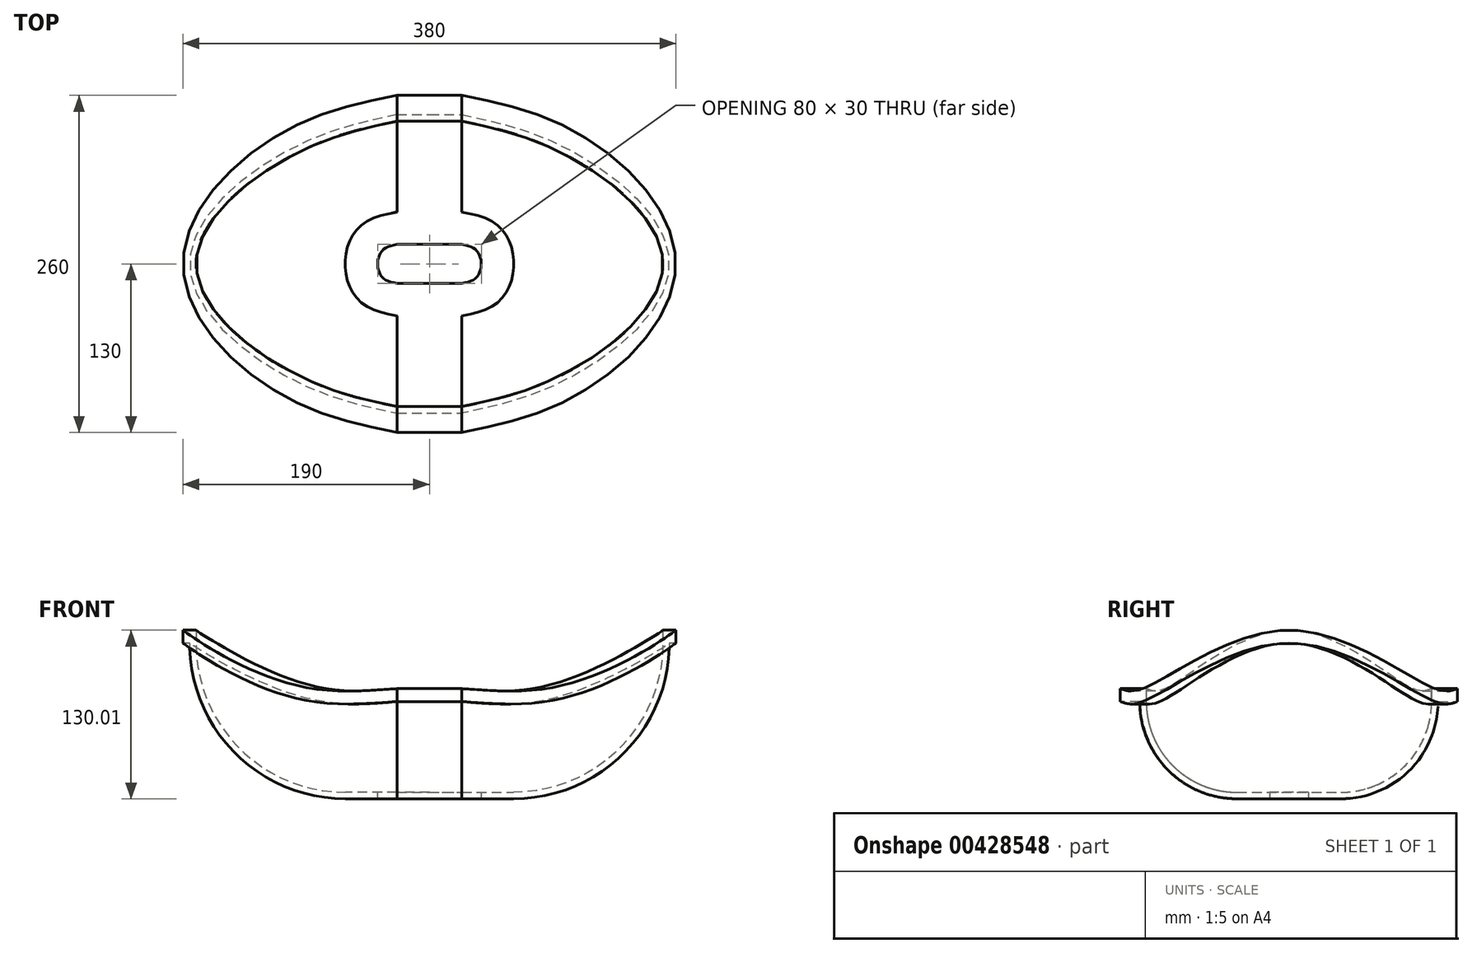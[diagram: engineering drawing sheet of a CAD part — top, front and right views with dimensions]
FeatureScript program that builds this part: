
annotation { "Feature Type Name" : "Feature", "Feature Type Description" : "" }
export const myFeature = defineFeature(function(context is Context, id is Id, definition is map)
    precondition{}
    {
        {
            var Q0;
            Q0=qCreatedBy(makeId("Front.planeOp"),FACE);
            var sketch = newSketch(context, id + "F0", { "sketchPlane" : qUnion([Q0])});
            skLineSegment(sketch, "E0.bottom", {"start": v(15, 5) * mm, "end": v(40, 5) * mm});
            skLineSegment(sketch, "E0.top", {"start": v(15, 0) * mm, "end": v(40, 0) * mm});
            skLineSegment(sketch, "E0.left", {"start": v(15, 5) * mm, "end": v(15, 0) * mm});
            skLineSegment(sketch, "E0.right", {"start": v(40, 5) * mm, "end": v(40, 0) * mm, "construction": true});
            skLineSegment(sketch, "E1.bottom", {"start": v(155, 130) * mm, "end": v(165, 130) * mm});
            skLineSegment(sketch, "E1.top", {"start": v(160, 120) * mm, "end": v(165, 120) * mm});
            skLineSegment(sketch, "E1.left", {"start": v(155, 130) * mm, "end": v(155, 120) * mm});
            skLineSegment(sketch, "E1.right", {"start": v(165, 130) * mm, "end": v(165, 120) * mm});
            skArc(sketch, "E2", {"start": v(40, 5) * mm, "mid": v(121.32, 38.68) * mm, "end": v(155, 120) * mm});
            skArc(sketch, "E3", {"start": v(40, 0) * mm, "mid": v(124.85, 35.15) * mm, "end": v(160, 120) * mm});
            skLineSegment(sketch, "E4", {"start": v(0, 0) * mm, "end": v(0, 50) * mm, "construction": true});
            skSolve(sketch);
        }
        {
            var Q0;
            Q0=sQuery(id+"F0.wireOp",EDGE,"E4");
            cPlane(context, id + "F1", {"entities" : qUnion([Q0]), "cplaneType" : CPlaneType.LINE_ANGLE, "offset" : 25 * mm, "angle" : 30 * degree, "oppositeDirection" : true, "width" : 150 * mm, "height" : 150 * mm});
        }
        {
            var Q0;
            Q0=qCreatedBy(id+"F1.planeOp",FACE);
            var sketch = newSketch(context, id + "F2", { "sketchPlane" : qUnion([Q0])});
            skLineSegment(sketch, "E5.bottom", {"start": v(15, 5) * mm, "end": v(40, 5) * mm});
            skLineSegment(sketch, "E5.top", {"start": v(15, 0) * mm, "end": v(40, 0) * mm});
            skLineSegment(sketch, "E5.left", {"start": v(15, 5) * mm, "end": v(15, 0) * mm});
            skLineSegment(sketch, "E5.right", {"start": v(40, 5) * mm, "end": v(40, 0) * mm, "construction": true});
            skLineSegment(sketch, "E6.bottom", {"start": v(110, 85) * mm, "end": v(130, 85) * mm});
            skLineSegment(sketch, "E6.top", {"start": v(115, 75) * mm, "end": v(130, 75) * mm});
            skLineSegment(sketch, "E6.left", {"start": v(110, 85) * mm, "end": v(110, 75) * mm});
            skLineSegment(sketch, "E6.right", {"start": v(130, 85) * mm, "end": v(130, 75) * mm});
            skArc(sketch, "E7", {"start": v(40, 5) * mm, "mid": v(89.5, 25.5) * mm, "end": v(110, 75) * mm});
            skArc(sketch, "E8", {"start": v(40, 0) * mm, "mid": v(93.03, 21.97) * mm, "end": v(115, 75) * mm});
            skLineSegment(sketch, "E9", {"start": v(0, 0) * mm, "end": v(0, 50) * mm, "construction": true});
            skSolve(sketch);
        }
        {
            var Q0;
            Q0=sQuery(id+"F2.wireOp",EDGE,"E9");
            cPlane(context, id + "F3", {"entities" : qUnion([Q0]), "cplaneType" : CPlaneType.LINE_ANGLE, "offset" : 25 * mm, "angle" : 150 * degree, "oppositeDirection" : true, "width" : 150 * mm, "height" : 150 * mm});
        }
        {
            var Q0;
            Q0=qCreatedBy(id+"F3.planeOp",FACE);
            var sketch = newSketch(context, id + "F4", { "sketchPlane" : qUnion([Q0])});
            skLineSegment(sketch, "E10.bottom", {"start": v(15, 5) * mm, "end": v(40, 5) * mm});
            skLineSegment(sketch, "E10.top", {"start": v(15, 0) * mm, "end": v(40, 0) * mm});
            skLineSegment(sketch, "E10.left", {"start": v(15, 5) * mm, "end": v(15, 0) * mm});
            skLineSegment(sketch, "E10.right", {"start": v(40, 5) * mm, "end": v(40, 0) * mm, "construction": true});
            skLineSegment(sketch, "E11.bottom", {"start": v(110, 85) * mm, "end": v(130, 85) * mm});
            skLineSegment(sketch, "E11.top", {"start": v(115, 75) * mm, "end": v(130, 75) * mm});
            skLineSegment(sketch, "E11.left", {"start": v(110, 85) * mm, "end": v(110, 75) * mm});
            skLineSegment(sketch, "E11.right", {"start": v(130, 85) * mm, "end": v(130, 75) * mm});
            skArc(sketch, "E12", {"start": v(40, 5) * mm, "mid": v(89.5, 25.5) * mm, "end": v(110, 75) * mm});
            skArc(sketch, "E13", {"start": v(40, 0) * mm, "mid": v(93.03, 21.97) * mm, "end": v(115, 75) * mm});
            skLineSegment(sketch, "E14", {"start": v(0, 0) * mm, "end": v(0, 50) * mm, "construction": true});
            skSolve(sketch);
        }
        {
            var Q0;
            Q0=qCreatedBy(makeId("Right.planeOp"),FACE);
            var sketch = newSketch(context, id + "F5", { "sketchPlane" : qUnion([Q0])});
            skLineSegment(sketch, "E15.bottom", {"start": v(15, 5) * mm, "end": v(40, 5) * mm});
            skLineSegment(sketch, "E15.top", {"start": v(15, 0) * mm, "end": v(40, 0) * mm});
            skLineSegment(sketch, "E15.left", {"start": v(15, 5) * mm, "end": v(15, 0) * mm});
            skLineSegment(sketch, "E15.right", {"start": v(40, 5) * mm, "end": v(40, 0) * mm, "construction": true});
            skLineSegment(sketch, "E16.bottom", {"start": v(110, 85) * mm, "end": v(130, 85) * mm});
            skLineSegment(sketch, "E16.top", {"start": v(115, 75) * mm, "end": v(130, 75) * mm});
            skLineSegment(sketch, "E16.left", {"start": v(110, 85) * mm, "end": v(110, 75) * mm});
            skLineSegment(sketch, "E16.right", {"start": v(130, 85) * mm, "end": v(130, 75) * mm});
            skArc(sketch, "E17", {"start": v(40, 5) * mm, "mid": v(89.5, 25.5) * mm, "end": v(110, 75) * mm});
            skArc(sketch, "E18", {"start": v(40, 0) * mm, "mid": v(93.03, 21.97) * mm, "end": v(115, 75) * mm});
            skLineSegment(sketch, "E19", {"start": v(0, 0) * mm, "end": v(0, 50) * mm, "construction": true});
            skSolve(sketch);
        }
        {
            var Q0;
            Q0=sQuery(id+"F5.wireOp",EDGE,"E19");
            cPlane(context, id + "F6", {"entities" : qUnion([Q0]), "cplaneType" : CPlaneType.LINE_ANGLE, "offset" : 25 * mm, "angle" : 180 * degree, "width" : 150 * mm, "height" : 150 * mm});
        }
        {
            var Q0;
            Q0=qCreatedBy(id+"F6.planeOp",FACE);
            var sketch = newSketch(context, id + "F7", { "sketchPlane" : qUnion([Q0])});
            skLineSegment(sketch, "E20.bottom", {"start": v(15, 5) * mm, "end": v(40, 5) * mm});
            skLineSegment(sketch, "E20.top", {"start": v(15, 0) * mm, "end": v(40, 0) * mm});
            skLineSegment(sketch, "E20.left", {"start": v(15, 5) * mm, "end": v(15, 0) * mm});
            skLineSegment(sketch, "E20.right", {"start": v(40, 5) * mm, "end": v(40, 0) * mm, "construction": true});
            skLineSegment(sketch, "E21.bottom", {"start": v(110, 85) * mm, "end": v(130, 85) * mm});
            skLineSegment(sketch, "E21.top", {"start": v(115, 75) * mm, "end": v(130, 75) * mm});
            skLineSegment(sketch, "E21.left", {"start": v(110, 85) * mm, "end": v(110, 75) * mm});
            skLineSegment(sketch, "E21.right", {"start": v(130, 85) * mm, "end": v(130, 75) * mm});
            skArc(sketch, "E22", {"start": v(40, 5) * mm, "mid": v(89.5, 25.5) * mm, "end": v(110, 75) * mm});
            skArc(sketch, "E23", {"start": v(40, 0) * mm, "mid": v(93.03, 21.97) * mm, "end": v(115, 75) * mm});
            skLineSegment(sketch, "E24", {"start": v(0, 0) * mm, "end": v(0, 50) * mm, "construction": true});
            skSolve(sketch);
        }
        {
            var Q0;
            Q0=makeQuery(id+"F5.imprint","IMPRINT",FACE,{"disambiguationData":[TD([[makeQuery(id+"F5.imprint","IMPRINT",EDGE,{"derivedFrom":sQuery(id+"F5.wireOp",EDGE,"E15.bottom")}),-1.0]])]});
            var Q1;
            Q1=makeQuery(id+"F2.imprint","IMPRINT",FACE,{"disambiguationData":[TD([[makeQuery(id+"F2.imprint","IMPRINT",EDGE,{"derivedFrom":sQuery(id+"F2.wireOp",EDGE,"E5.bottom")}),-1.0]])]});
            var Q2;
            Q2=makeQuery(id+"F0.imprint","IMPRINT",FACE,{"disambiguationData":[TD([[makeQuery(id+"F0.imprint","IMPRINT",EDGE,{"derivedFrom":sQuery(id+"F0.wireOp",EDGE,"E0.bottom")}),-1.0]])]});
            var Q3;
            Q3=makeQuery(id+"F4.imprint","IMPRINT",FACE,{"disambiguationData":[TD([[makeQuery(id+"F4.imprint","IMPRINT",EDGE,{"derivedFrom":sQuery(id+"F4.wireOp",EDGE,"E10.bottom")}),-1.0]])]});
            var Q4;
            Q4=makeQuery(id+"F7.imprint","IMPRINT",FACE,{"disambiguationData":[TD([[makeQuery(id+"F7.imprint","IMPRINT",EDGE,{"derivedFrom":sQuery(id+"F7.wireOp",EDGE,"E20.bottom")}),-1.0]])]});
            loft(context, id + "F8", {"sheetProfilesArray" : [{ "sheetProfileEntities" : qUnion([Q0]) }, { "sheetProfileEntities" : qUnion([Q1]) }, { "sheetProfileEntities" : qUnion([Q2]) }, { "sheetProfileEntities" : qUnion([Q3]) }, { "sheetProfileEntities" : qUnion([Q4]) }]});
        }
        {
            var Q0;
            Q0=makeQuery(id+"F8.opLoft","CAP_FACE",FACE,{"disambiguationData":[OSD([makeQuery(id+"F5.imprint","IMPRINT",FACE,{"disambiguationData":[TD([[makeQuery(id+"F5.imprint","IMPRINT",EDGE,{"derivedFrom":sQuery(id+"F5.wireOp",EDGE,"E15.bottom")}),-1.0]])]})])],"isStart":true});
            var sketch = newSketch(context, id + "F9", { "sketchPlane" : qUnion([Q0])});
            skLineSegment(sketch, "E25.0.0", {"start": v(-130, 75) * mm, "end": v(-130, 85) * mm});
            skLineSegment(sketch, "E25.0.1", {"start": v(-130, 75) * mm, "end": v(-115, 75) * mm});
            skFitSpline(sketch, "E25.0.2", {"points": [v(-115, 75) * mm, v(-115, 72.54) * mm, v(-114.88, 70.1) * mm, v(-114.64, 67.65) * mm, v(-114.4, 65.2) * mm, v(-114.04, 62.78) * mm, v(-113.56, 60.37) * mm, v(-113.08, 57.96) * mm, v(-112.48, 55.58) * mm, v(-111.77, 53.23) * mm, v(-111.06, 50.88) * mm, v(-110.23, 48.57) * mm, v(-109.3, 46.3) * mm, v(-108.35, 44.03) * mm, v(-107.3, 41.81) * mm, v(-106.14, 39.65) * mm, v(-104.99, 37.48) * mm, v(-103.73, 35.37) * mm, v(-102.36, 33.33) * mm, v(-101, 31.3) * mm, v(-99.53, 29.32) * mm, v(-97.98, 27.42) * mm, v(-96.42, 25.52) * mm, v(-94.77, 23.7) * mm, v(-93.03, 21.97) * mm, v(-91.3, 20.23) * mm, v(-89.48, 18.58) * mm, v(-87.58, 17.02) * mm, v(-85.68, 15.47) * mm, v(-83.71, 14) * mm, v(-81.67, 12.64) * mm, v(-79.63, 11.28) * mm, v(-77.52, 10.01) * mm, v(-75.35, 8.86) * mm, v(-73.19, 7.7) * mm, v(-70.97, 6.65) * mm, v(-68.7, 5.7) * mm, v(-66.43, 4.77) * mm, v(-64.12, 3.94) * mm, v(-61.77, 3.23) * mm, v(-59.42, 2.52) * mm, v(-57.04, 1.92) * mm, v(-54.63, 1.44) * mm, v(-52.22, 0.96) * mm, v(-49.8, 0.6) * mm, v(-47.35, 0.36) * mm, v(-44.9, 0.12) * mm, v(-42.46, 0) * mm, v(-40, 0) * mm]});
            skLineSegment(sketch, "E25.0.3", {"start": v(-40, 0) * mm, "end": v(-15, 0) * mm});
            skLineSegment(sketch, "E25.0.4", {"start": v(-15, 0) * mm, "end": v(-15, 5) * mm});
            skLineSegment(sketch, "E25.0.5", {"start": v(-40, 5) * mm, "end": v(-15, 5) * mm});
            skFitSpline(sketch, "E25.0.6", {"points": [v(-40, 5) * mm, v(-42.3, 5) * mm, v(-44.58, 5.11) * mm, v(-46.86, 5.34) * mm, v(-49.14, 5.56) * mm, v(-51.4, 5.9) * mm, v(-53.66, 6.35) * mm, v(-55.9, 6.8) * mm, v(-58.13, 7.35) * mm, v(-60.32, 8.01) * mm, v(-62.51, 8.68) * mm, v(-64.67, 9.45) * mm, v(-66.79, 10.33) * mm, v(-68.9, 11.2) * mm, v(-70.98, 12.18) * mm, v(-73, 13.27) * mm, v(-75.02, 14.35) * mm, v(-76.98, 15.52) * mm, v(-78.89, 16.8) * mm, v(-80.8, 18.07) * mm, v(-82.64, 19.43) * mm, v(-84.4, 20.89) * mm, v(-86.18, 22.34) * mm, v(-87.88, 23.88) * mm, v(-89.5, 25.5) * mm, v(-91.12, 27.12) * mm, v(-92.66, 28.82) * mm, v(-94.11, 30.6) * mm, v(-95.56, 32.36) * mm, v(-96.93, 34.2) * mm, v(-98.2, 36.11) * mm, v(-99.48, 38.02) * mm, v(-100.65, 39.98) * mm, v(-101.73, 42) * mm, v(-102.82, 44.02) * mm, v(-103.8, 46.1) * mm, v(-104.67, 48.21) * mm, v(-105.55, 50.33) * mm, v(-106.32, 52.49) * mm, v(-106.99, 54.68) * mm, v(-107.65, 56.87) * mm, v(-108.2, 59.1) * mm, v(-108.65, 61.34) * mm, v(-109.1, 63.6) * mm, v(-109.44, 65.86) * mm, v(-109.66, 68.14) * mm, v(-109.89, 70.42) * mm, v(-110, 72.7) * mm, v(-110, 75) * mm]});
            skFitSpline(sketch, "E25.0.7", {"points": [v(-110, 75) * mm, v(-110, 78.33) * mm, v(-110, 81.67) * mm, v(-110, 85) * mm]});
            skLineSegment(sketch, "E25.0.8", {"start": v(-130, 85) * mm, "end": v(-110, 85) * mm});
            skLineSegment(sketch, "E26.0.0", {"start": v(130, 75) * mm, "end": v(130, 85) * mm});
            skLineSegment(sketch, "E26.0.1", {"start": v(130, 85) * mm, "end": v(110, 85) * mm});
            skFitSpline(sketch, "E26.0.2", {"points": [v(110, 85) * mm, v(110, 81.67) * mm, v(110, 78.33) * mm, v(110, 75) * mm]});
            skFitSpline(sketch, "E26.0.3", {"points": [v(110, 75) * mm, v(110, 72.7) * mm, v(109.89, 70.42) * mm, v(109.66, 68.14) * mm, v(109.44, 65.86) * mm, v(109.1, 63.6) * mm, v(108.65, 61.34) * mm, v(108.2, 59.1) * mm, v(107.65, 56.87) * mm, v(106.99, 54.68) * mm, v(106.32, 52.49) * mm, v(105.55, 50.33) * mm, v(104.67, 48.21) * mm, v(103.8, 46.1) * mm, v(102.82, 44.02) * mm, v(101.73, 42) * mm, v(100.65, 39.98) * mm, v(99.48, 38.02) * mm, v(98.2, 36.11) * mm, v(96.93, 34.2) * mm, v(95.57, 32.36) * mm, v(94.11, 30.6) * mm, v(92.66, 28.82) * mm, v(91.12, 27.12) * mm, v(89.5, 25.5) * mm, v(87.88, 23.88) * mm, v(86.18, 22.34) * mm, v(84.4, 20.89) * mm, v(82.64, 19.44) * mm, v(80.8, 18.07) * mm, v(78.89, 16.8) * mm, v(76.98, 15.52) * mm, v(75.02, 14.35) * mm, v(73, 13.27) * mm, v(70.98, 12.18) * mm, v(68.9, 11.2) * mm, v(66.79, 10.33) * mm, v(64.67, 9.45) * mm, v(62.51, 8.68) * mm, v(60.32, 8.01) * mm, v(58.13, 7.35) * mm, v(55.9, 6.8) * mm, v(53.66, 6.35) * mm, v(51.4, 5.9) * mm, v(49.14, 5.56) * mm, v(46.86, 5.34) * mm, v(44.58, 5.11) * mm, v(42.3, 5) * mm, v(40, 5) * mm]});
            skLineSegment(sketch, "E26.0.4", {"start": v(40, 5) * mm, "end": v(15, 5) * mm});
            skLineSegment(sketch, "E26.0.5", {"start": v(15, 5) * mm, "end": v(15, 0) * mm});
            skLineSegment(sketch, "E26.0.6", {"start": v(15, 0) * mm, "end": v(40, 0) * mm});
            skFitSpline(sketch, "E26.0.7", {"points": [v(40, 0) * mm, v(42.46, 0) * mm, v(44.9, 0.12) * mm, v(47.35, 0.36) * mm, v(49.8, 0.6) * mm, v(52.22, 0.96) * mm, v(54.63, 1.44) * mm, v(57.04, 1.92) * mm, v(59.42, 2.52) * mm, v(61.77, 3.23) * mm, v(64.12, 3.94) * mm, v(66.43, 4.77) * mm, v(68.7, 5.7) * mm, v(70.97, 6.65) * mm, v(73.19, 7.7) * mm, v(75.35, 8.86) * mm, v(77.52, 10.01) * mm, v(79.63, 11.27) * mm, v(81.67, 12.64) * mm, v(83.7, 14) * mm, v(85.68, 15.47) * mm, v(87.58, 17.02) * mm, v(89.48, 18.58) * mm, v(91.3, 20.23) * mm, v(93.03, 21.97) * mm, v(94.77, 23.7) * mm, v(96.42, 25.52) * mm, v(97.98, 27.42) * mm, v(99.53, 29.32) * mm, v(101, 31.29) * mm, v(102.36, 33.33) * mm, v(103.72, 35.37) * mm, v(104.99, 37.48) * mm, v(106.14, 39.65) * mm, v(107.3, 41.81) * mm, v(108.35, 44.03) * mm, v(109.3, 46.3) * mm, v(110.23, 48.57) * mm, v(111.06, 50.88) * mm, v(111.77, 53.23) * mm, v(112.48, 55.58) * mm, v(113.08, 57.96) * mm, v(113.56, 60.37) * mm, v(114.04, 62.78) * mm, v(114.4, 65.2) * mm, v(114.64, 67.65) * mm, v(114.88, 70.1) * mm, v(115, 72.54) * mm, v(115, 75) * mm]});
            skLineSegment(sketch, "E26.0.8", {"start": v(115, 75) * mm, "end": v(130, 75) * mm});
            skSolve(sketch);
        }
        {
            var Q0;
            Q0=makeQuery(id+"F9.imprint","IMPRINT",FACE,{"disambiguationData":[TD([[makeQuery(id+"F9.imprint","IMPRINT",EDGE,{"derivedFrom":sQuery(id+"F9.wireOp",EDGE,"E25.0.0")}),-1.0]])]});
            var Q1;
            Q1=makeQuery(id+"F9.imprint","IMPRINT",FACE,{"disambiguationData":[TD([[makeQuery(id+"F9.imprint","IMPRINT",EDGE,{"derivedFrom":sQuery(id+"F9.wireOp",EDGE,"E26.0.0")}),1.0]])]});
            extrude(context, id + "F10", {"entities" : qUnion([Q0, Q1]), "operationType" : NewBodyOperationType.ADD, "depth" : 25 * mm});
        }
        {
            var Q0;
            Q0=makeQuery(id+"F8.opLoft","SWEPT_BODY",BODY,{"disambiguationData":[OSD([sQuery(id+"F0.wireOp",EDGE,"E3"),sQuery(id+"F2.wireOp",EDGE,"E8"),sQuery(id+"F4.wireOp",EDGE,"E13"),makeQuery(id+"F5.imprint","IMPRINT",FACE,{"disambiguationData":[TD([[makeQuery(id+"F5.imprint","IMPRINT",EDGE,{"derivedFrom":sQuery(id+"F5.wireOp",EDGE,"E15.bottom")}),-1.0]])]}),makeQuery(id+"F7.imprint","IMPRINT",FACE,{"disambiguationData":[TD([[makeQuery(id+"F7.imprint","IMPRINT",EDGE,{"derivedFrom":sQuery(id+"F7.wireOp",EDGE,"E20.bottom")}),-1.0]])]})])]});
            var Q1;
            Q1=makeQuery(id+"F10.opExtrude","CAP_FACE",FACE,{"disambiguationData":[OSD([sQuery(id+"F9.wireOp",EDGE,"E25.0.0"),sQuery(id+"F9.wireOp",EDGE,"E25.0.1"),sQuery(id+"F9.wireOp",EDGE,"E25.0.2"),sQuery(id+"F9.wireOp",EDGE,"E25.0.3"),sQuery(id+"F9.wireOp",EDGE,"E25.0.4"),sQuery(id+"F9.wireOp",EDGE,"E25.0.5"),sQuery(id+"F9.wireOp",EDGE,"E25.0.6"),sQuery(id+"F9.wireOp",EDGE,"E25.0.7"),sQuery(id+"F9.wireOp",EDGE,"E25.0.8")])],"isStart":false});
            mirror(context, id + "F11", {"operationType" : NewBodyOperationType.ADD, "entities" : qUnion([Q0]), "mirrorPlane" : qUnion([Q1])});
        }
    });
